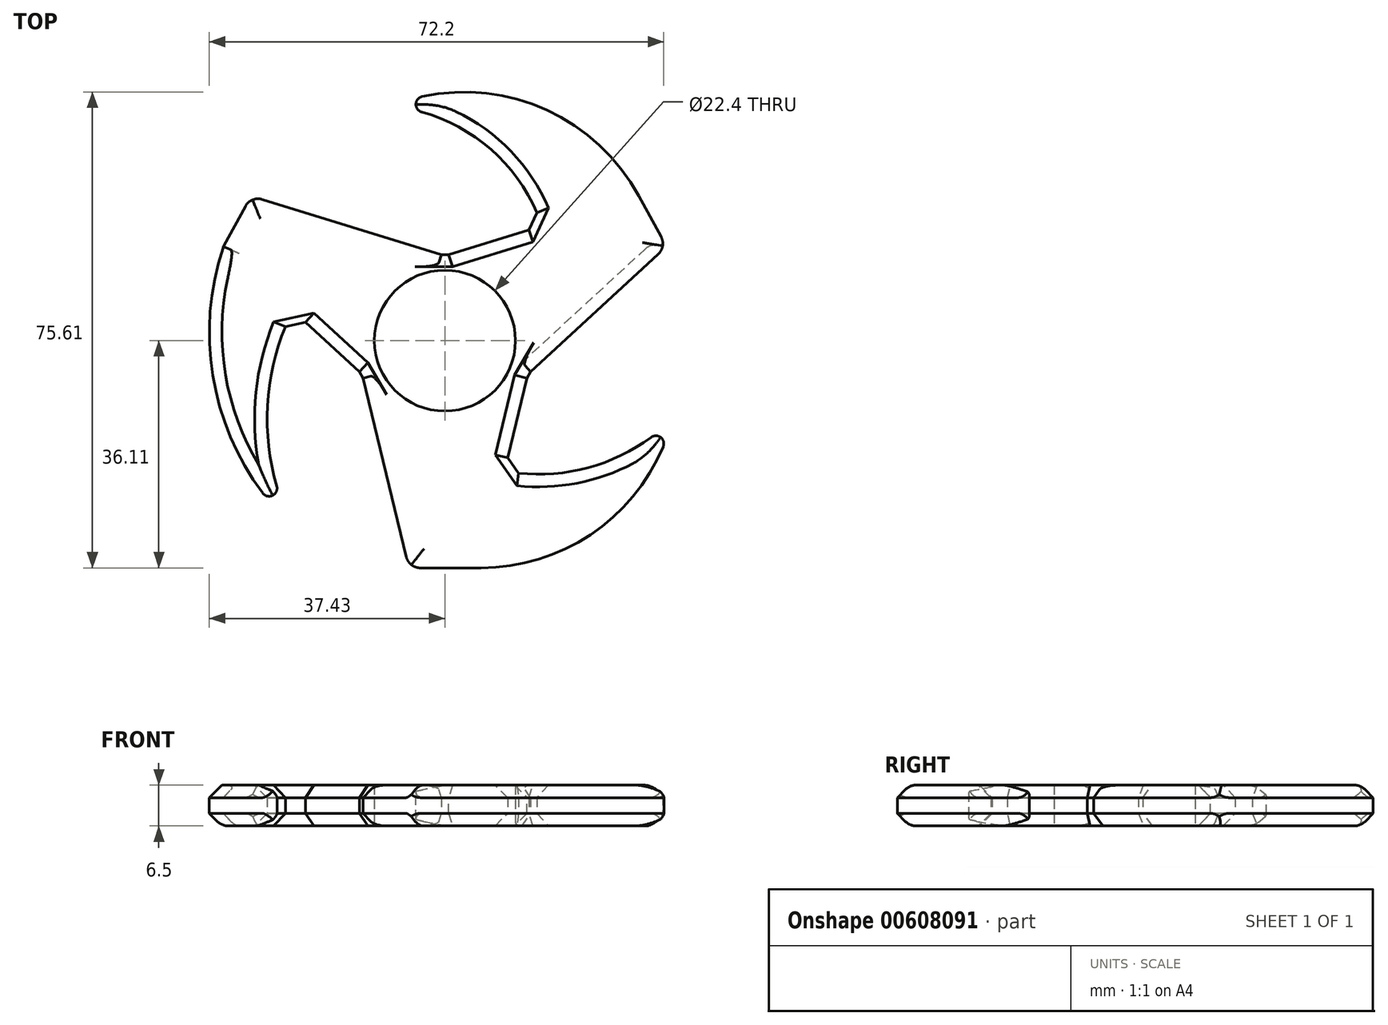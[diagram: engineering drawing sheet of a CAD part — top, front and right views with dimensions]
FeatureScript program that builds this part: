
annotation { "Feature Type Name" : "Feature", "Feature Type Description" : "" }
export const myFeature = defineFeature(function(context is Context, id is Id, definition is map)
    precondition{}
    {
        {
            var Q0;
            Q0=qCreatedBy(makeId("Top.planeOp"),FACE);
            var sketch = newSketch(context, id + "F0", { "sketchPlane" : qUnion([Q0])});
            skCircle(sketch, "E0", {"center": v(0, 0) * mm, "radius": 47.37 * mm});
            skPoint(sketch, "E1.0.midPoint", {"position": v(0, 23) * mm});
            skLineSegment(sketch, "E2", {"start": v(-5.71, -36.1) * mm, "end": v(0, -36.1) * mm});
            skLineSegment(sketch, "E3", {"start": v(-30.81, 23) * mm, "end": v(-35.2, 14.95) * mm});
            skLineSegment(sketch, "E4.MirrorCS", {"start": v(30.81, 23) * mm, "end": v(35.2, 14.95) * mm});
            skLineSegment(sketch, "E5.MirrorCS", {"start": v(5.71, -36.1) * mm, "end": v(0, -36.1) * mm});
            skLineSegment(sketch, "E6", {"start": v(0, -46) * mm, "end": v(0, 0) * mm});
            skLineSegment(sketch, "E7", {"start": v(-13.16, -5.35) * mm, "end": v(-5.71, -36.1) * mm});
            skLineSegment(sketch, "E8", {"start": v(-30.81, 23) * mm, "end": v(0, 13.45) * mm});
            skLineSegment(sketch, "E9", {"start": v(0, 59.17) * mm, "end": v(0, -57.43) * mm, "construction": true});
            skLineSegment(sketch, "E10.MirrorCS", {"start": v(35.2, 14.95) * mm, "end": v(13.16, -5.35) * mm});
            skCircle(sketch, "E11", {"center": v(0, 0) * mm, "radius": 11.2 * mm});
            skArc(sketch, "E12", {"start": v(-24.18, 4.8) * mm, "mid": v(-28.24, -12.41) * mm, "end": v(-24.18, -29.62) * mm});
            skArc(sketch, "E13", {"start": v(-35.2, 14.95) * mm, "mid": v(-36.18, -8.94) * mm, "end": v(-24.18, -29.62) * mm});
            skLineSegment(sketch, "E14", {"start": v(-24.18, 4.8) * mm, "end": v(-13.16, -5.35) * mm});
            skArc(sketch, "E15", {"start": v(9.44, -20.73) * mm, "mid": v(23.83, -19.87) * mm, "end": v(36.17, -12.41) * mm});
            skArc(sketch, "E16", {"start": v(5.71, -36.1) * mm, "mid": v(25, -29.49) * mm, "end": v(36.17, -12.41) * mm});
            skLineSegment(sketch, "E17", {"start": v(9.44, -20.73) * mm, "end": v(13.16, -5.35) * mm});
            skArc(sketch, "E18", {"start": v(15.4, 18.23) * mm, "mid": v(6.18, 31.3) * mm, "end": v(-8.69, 37.24) * mm});
            skArc(sketch, "E19", {"start": v(30.81, 23) * mm, "mid": v(13.77, 37.63) * mm, "end": v(-8.69, 37.24) * mm});
            skLineSegment(sketch, "E20", {"start": v(15.4, 18.23) * mm, "end": v(0, 13.45) * mm});
            skSolve(sketch);
        }
        {
            var Q0;
            Q0=makeQuery(id+"F0.imprint","IMPRINT",FACE,{"disambiguationData":[TD([[makeQuery(id+"F0.imprint","IMPRINT",EDGE,{"derivedFrom":sQuery(id+"F0.wireOp",EDGE,"E2")}),1.0]])]});
            extrude(context, id + "F1", {"entities" : qUnion([Q0]), "depth" : 6.5 * mm, "offsetDistance" : 25.4 * mm});
        }
        {
            var Q0;
            Q0=makeQuery(id+"F1.opExtrude","CAP_EDGE",EDGE,{"disambiguationData":[OSD([sQuery(id+"F0.wireOp",EDGE,"E3")])],"isStart":false});
            var Q1;
            Q1=makeQuery(id+"F1.opExtrude","CAP_EDGE",EDGE,{"disambiguationData":[OSD([sQuery(id+"F0.wireOp",EDGE,"E3")])],"isStart":true});
            var Q2;
            Q2=makeQuery(id+"F1.opExtrude","CAP_EDGE",EDGE,{"disambiguationData":[OSD([sQuery(id+"F0.wireOp",EDGE,"E8")])],"isStart":false});
            var Q3;
            Q3=makeQuery(id+"F1.opExtrude","CAP_EDGE",EDGE,{"disambiguationData":[OSD([sQuery(id+"F0.wireOp",EDGE,"E8")])],"isStart":true});
            var Q4;
            Q4=makeQuery(id+"F1.opExtrude","CAP_EDGE",EDGE,{"disambiguationData":[OSD([sQuery(id+"F0.wireOp",EDGE,"abd28260-5241-46c7-9a49-41b6c746b0a20.MirrorCS")])],"isStart":true});
            var Q5;
            Q5=makeQuery(id+"F1.opExtrude","CAP_EDGE",EDGE,{"disambiguationData":[OSD([sQuery(id+"F0.wireOp",EDGE,"abd28260-5241-46c7-9a49-41b6c746b0a20.MirrorCS")])],"isStart":false});
            var Q6;
            Q6=makeQuery(id+"F1.opExtrude","CAP_EDGE",EDGE,{"disambiguationData":[OSD([sQuery(id+"F0.wireOp",EDGE,"E4.MirrorCS")])],"isStart":false});
            var Q7;
            Q7=makeQuery(id+"F1.opExtrude","CAP_EDGE",EDGE,{"disambiguationData":[OSD([sQuery(id+"F0.wireOp",EDGE,"QS45Ad1f-zS77-PmQo-UpQF-622HsvFARksc")])],"isStart":false});
            var Q8;
            Q8=makeQuery(id+"F1.opExtrude","CAP_EDGE",EDGE,{"disambiguationData":[OSD([sQuery(id+"F0.wireOp",EDGE,"E7")])],"isStart":false});
            var Q9;
            Q9=makeQuery(id+"F1.opExtrude","CAP_EDGE",EDGE,{"disambiguationData":[OSD([sQuery(id+"F0.wireOp",EDGE,"E7")])],"isStart":true});
            var Q10;
            Q10=makeQuery(id+"F1.opExtrude","CAP_EDGE",EDGE,{"disambiguationData":[OSD([sQuery(id+"F0.wireOp",EDGE,"E2"),sQuery(id+"F0.wireOp",EDGE,"E5.MirrorCS")])],"isStart":false});
            var Q11;
            Q11=makeQuery(id+"F1.opExtrude","CAP_EDGE",EDGE,{"disambiguationData":[OSD([sQuery(id+"F0.wireOp",EDGE,"273b9097-7943-4664-901e-a9dfdd62f2f80.MirrorCS")])],"isStart":false});
            var Q12;
            Q12=makeQuery(id+"F1.opExtrude","CAP_EDGE",EDGE,{"disambiguationData":[OSD([sQuery(id+"F0.wireOp",EDGE,"E10.MirrorCS")])],"isStart":false});
            var Q13;
            Q13=makeQuery(id+"F1.opExtrude","CAP_EDGE",EDGE,{"disambiguationData":[OSD([sQuery(id+"F0.wireOp",EDGE,"QS45Ad1f-zS77-PmQo-UpQF-622HsvFARksc")])],"isStart":true});
            var Q14;
            Q14=makeQuery(id+"F1.opExtrude","CAP_EDGE",EDGE,{"disambiguationData":[OSD([sQuery(id+"F0.wireOp",EDGE,"E2"),sQuery(id+"F0.wireOp",EDGE,"E5.MirrorCS")])],"isStart":true});
            var Q15;
            Q15=makeQuery(id+"F1.opExtrude","CAP_EDGE",EDGE,{"disambiguationData":[OSD([sQuery(id+"F0.wireOp",EDGE,"273b9097-7943-4664-901e-a9dfdd62f2f80.MirrorCS")])],"isStart":true});
            var Q16;
            Q16=makeQuery(id+"F1.opExtrude","CAP_EDGE",EDGE,{"disambiguationData":[OSD([sQuery(id+"F0.wireOp",EDGE,"E10.MirrorCS")])],"isStart":true});
            var Q17;
            Q17=makeQuery(id+"F1.opExtrude","CAP_EDGE",EDGE,{"disambiguationData":[OSD([sQuery(id+"F0.wireOp",EDGE,"E4.MirrorCS")])],"isStart":true});
            var Q18;
            Q18=makeQuery(id+"F1.opExtrude","CAP_EDGE",EDGE,{"disambiguationData":[OSD([sQuery(id+"F0.wireOp",EDGE,"E12")])],"isStart":false});
            var Q19;
            Q19=makeQuery(id+"F1.opExtrude","CAP_EDGE",EDGE,{"disambiguationData":[OSD([sQuery(id+"F0.wireOp",EDGE,"E12")])],"isStart":true});
            var Q20;
            Q20=makeQuery(id+"F1.opExtrude","CAP_EDGE",EDGE,{"disambiguationData":[OSD([sQuery(id+"F0.wireOp",EDGE,"E18")])],"isStart":false});
            var Q21;
            Q21=makeQuery(id+"F1.opExtrude","CAP_EDGE",EDGE,{"disambiguationData":[OSD([sQuery(id+"F0.wireOp",EDGE,"E18")])],"isStart":true});
            var Q22;
            Q22=makeQuery(id+"F1.opExtrude","CAP_EDGE",EDGE,{"disambiguationData":[OSD([sQuery(id+"F0.wireOp",EDGE,"E15")])],"isStart":false});
            var Q23;
            Q23=makeQuery(id+"F1.opExtrude","CAP_EDGE",EDGE,{"disambiguationData":[OSD([sQuery(id+"F0.wireOp",EDGE,"E15")])],"isStart":true});
            var Q24;
            Q24=makeQuery(id+"F1.opExtrude","CAP_EDGE",EDGE,{"disambiguationData":[OSD([sQuery(id+"F0.wireOp",EDGE,"E13")])],"isStart":true});
            var Q25;
            Q25=makeQuery(id+"F1.opExtrude","CAP_EDGE",EDGE,{"disambiguationData":[OSD([sQuery(id+"F0.wireOp",EDGE,"E13")])],"isStart":false});
            var Q26;
            Q26=makeQuery(id+"F1.opExtrude","SWEPT_FACE",FACE,{"disambiguationData":[OSD([sQuery(id+"F0.wireOp",EDGE,"E14")])]});
            var Q27;
            Q27=makeQuery(id+"F1.opExtrude","SWEPT_FACE",FACE,{"disambiguationData":[OSD([sQuery(id+"F0.wireOp",EDGE,"E17")])]});
            var Q28;
            Q28=makeQuery(id+"F1.opExtrude","SWEPT_FACE",FACE,{"disambiguationData":[OSD([sQuery(id+"F0.wireOp",EDGE,"E20")])]});
            chamfer(context, id + "F2", {"entities" : qUnion([Q0, Q1, Q2, Q3, Q4, Q5, Q6, Q7, Q8, Q9, Q10, Q11, Q12, Q13, Q14, Q15, Q16, Q17, Q18, Q19, Q20, Q21, Q22, Q23, Q24, Q25, Q26, Q27, Q28]), "width" : 2 * mm, "tangentPropagation" : true});
        }
        {
            var Q0;
            {var subQ0=sQuery(id+"F0.wireOp",EDGE,"E3");Q0=makeQuery(id+"F2.opChamfer","BLEND_EDGE",EDGE,{"blendedFrom":[makeQuery(id+"F1.opExtrude","CAP_EDGE",EDGE,{"disambiguationData":[OSD([subQ0])],"isStart":false}),makeQuery(id+"F1.opExtrude","CAP_FACE",FACE,{"disambiguationData":[OSD([sQuery(id+"F0.wireOp",EDGE,"E2"),subQ0,sQuery(id+"F0.wireOp",EDGE,"E4.MirrorCS"),sQuery(id+"F0.wireOp",EDGE,"E5.MirrorCS"),sQuery(id+"F0.wireOp",EDGE,"QS45Ad1f-zS77-PmQo-UpQF-622HsvFARksc"),sQuery(id+"F0.wireOp",EDGE,"E7"),sQuery(id+"F0.wireOp",EDGE,"E8"),sQuery(id+"F0.wireOp",EDGE,"abd28260-5241-46c7-9a49-41b6c746b0a20.MirrorCS"),sQuery(id+"F0.wireOp",EDGE,"E10.MirrorCS"),sQuery(id+"F0.wireOp",EDGE,"273b9097-7943-4664-901e-a9dfdd62f2f80.MirrorCS"),sQuery(id+"F0.wireOp",EDGE,"E11")])],"isStart":false})],"blendedInto":[makeQuery(id+"F1.opExtrude","CAP_FACE",FACE,{"disambiguationData":[OSD([sQuery(id+"F0.wireOp",EDGE,"E2"),subQ0,sQuery(id+"F0.wireOp",EDGE,"E4.MirrorCS"),sQuery(id+"F0.wireOp",EDGE,"E5.MirrorCS"),sQuery(id+"F0.wireOp",EDGE,"QS45Ad1f-zS77-PmQo-UpQF-622HsvFARksc"),sQuery(id+"F0.wireOp",EDGE,"E7"),sQuery(id+"F0.wireOp",EDGE,"E8"),sQuery(id+"F0.wireOp",EDGE,"abd28260-5241-46c7-9a49-41b6c746b0a20.MirrorCS"),sQuery(id+"F0.wireOp",EDGE,"E10.MirrorCS"),sQuery(id+"F0.wireOp",EDGE,"273b9097-7943-4664-901e-a9dfdd62f2f80.MirrorCS"),sQuery(id+"F0.wireOp",EDGE,"E11")])],"isStart":false})]});}
            var Q1;
            {var subQ0=sQuery(id+"F0.wireOp",EDGE,"abd28260-5241-46c7-9a49-41b6c746b0a20.MirrorCS");Q1=makeQuery(id+"F2.opChamfer","BLEND_EDGE",EDGE,{"blendedFrom":[makeQuery(id+"F1.opExtrude","CAP_EDGE",EDGE,{"disambiguationData":[OSD([subQ0])],"isStart":false}),makeQuery(id+"F1.opExtrude","CAP_FACE",FACE,{"disambiguationData":[OSD([sQuery(id+"F0.wireOp",EDGE,"E2"),sQuery(id+"F0.wireOp",EDGE,"E3"),sQuery(id+"F0.wireOp",EDGE,"E4.MirrorCS"),sQuery(id+"F0.wireOp",EDGE,"E5.MirrorCS"),sQuery(id+"F0.wireOp",EDGE,"QS45Ad1f-zS77-PmQo-UpQF-622HsvFARksc"),sQuery(id+"F0.wireOp",EDGE,"E7"),sQuery(id+"F0.wireOp",EDGE,"E8"),subQ0,sQuery(id+"F0.wireOp",EDGE,"E10.MirrorCS"),sQuery(id+"F0.wireOp",EDGE,"273b9097-7943-4664-901e-a9dfdd62f2f80.MirrorCS"),sQuery(id+"F0.wireOp",EDGE,"E11")])],"isStart":false})],"blendedInto":[makeQuery(id+"F1.opExtrude","CAP_FACE",FACE,{"disambiguationData":[OSD([sQuery(id+"F0.wireOp",EDGE,"E2"),sQuery(id+"F0.wireOp",EDGE,"E3"),sQuery(id+"F0.wireOp",EDGE,"E4.MirrorCS"),sQuery(id+"F0.wireOp",EDGE,"E5.MirrorCS"),sQuery(id+"F0.wireOp",EDGE,"QS45Ad1f-zS77-PmQo-UpQF-622HsvFARksc"),sQuery(id+"F0.wireOp",EDGE,"E7"),sQuery(id+"F0.wireOp",EDGE,"E8"),subQ0,sQuery(id+"F0.wireOp",EDGE,"E10.MirrorCS"),sQuery(id+"F0.wireOp",EDGE,"273b9097-7943-4664-901e-a9dfdd62f2f80.MirrorCS"),sQuery(id+"F0.wireOp",EDGE,"E11")])],"isStart":false})]});}
            var Q2;
            {var subQ0=sQuery(id+"F0.wireOp",EDGE,"E8");Q2=makeQuery(id+"F2.opChamfer","BLEND_EDGE",EDGE,{"blendedFrom":[makeQuery(id+"F1.opExtrude","CAP_EDGE",EDGE,{"disambiguationData":[OSD([subQ0])],"isStart":false}),makeQuery(id+"F1.opExtrude","CAP_FACE",FACE,{"disambiguationData":[OSD([sQuery(id+"F0.wireOp",EDGE,"E2"),sQuery(id+"F0.wireOp",EDGE,"E3"),sQuery(id+"F0.wireOp",EDGE,"E4.MirrorCS"),sQuery(id+"F0.wireOp",EDGE,"E5.MirrorCS"),sQuery(id+"F0.wireOp",EDGE,"QS45Ad1f-zS77-PmQo-UpQF-622HsvFARksc"),sQuery(id+"F0.wireOp",EDGE,"E7"),subQ0,sQuery(id+"F0.wireOp",EDGE,"abd28260-5241-46c7-9a49-41b6c746b0a20.MirrorCS"),sQuery(id+"F0.wireOp",EDGE,"E10.MirrorCS"),sQuery(id+"F0.wireOp",EDGE,"273b9097-7943-4664-901e-a9dfdd62f2f80.MirrorCS"),sQuery(id+"F0.wireOp",EDGE,"E11")])],"isStart":false})],"blendedInto":[makeQuery(id+"F1.opExtrude","CAP_FACE",FACE,{"disambiguationData":[OSD([sQuery(id+"F0.wireOp",EDGE,"E2"),sQuery(id+"F0.wireOp",EDGE,"E3"),sQuery(id+"F0.wireOp",EDGE,"E4.MirrorCS"),sQuery(id+"F0.wireOp",EDGE,"E5.MirrorCS"),sQuery(id+"F0.wireOp",EDGE,"QS45Ad1f-zS77-PmQo-UpQF-622HsvFARksc"),sQuery(id+"F0.wireOp",EDGE,"E7"),subQ0,sQuery(id+"F0.wireOp",EDGE,"abd28260-5241-46c7-9a49-41b6c746b0a20.MirrorCS"),sQuery(id+"F0.wireOp",EDGE,"E10.MirrorCS"),sQuery(id+"F0.wireOp",EDGE,"273b9097-7943-4664-901e-a9dfdd62f2f80.MirrorCS"),sQuery(id+"F0.wireOp",EDGE,"E11")])],"isStart":false})]});}
            var Q3;
            {var subQ0=sQuery(id+"F0.wireOp",EDGE,"E10.MirrorCS");Q3=makeQuery(id+"F2.opChamfer","BLEND_EDGE",EDGE,{"blendedFrom":[makeQuery(id+"F1.opExtrude","CAP_EDGE",EDGE,{"disambiguationData":[OSD([subQ0])],"isStart":false}),makeQuery(id+"F1.opExtrude","CAP_FACE",FACE,{"disambiguationData":[OSD([sQuery(id+"F0.wireOp",EDGE,"E2"),sQuery(id+"F0.wireOp",EDGE,"E3"),sQuery(id+"F0.wireOp",EDGE,"E4.MirrorCS"),sQuery(id+"F0.wireOp",EDGE,"E5.MirrorCS"),sQuery(id+"F0.wireOp",EDGE,"QS45Ad1f-zS77-PmQo-UpQF-622HsvFARksc"),sQuery(id+"F0.wireOp",EDGE,"E7"),sQuery(id+"F0.wireOp",EDGE,"E8"),sQuery(id+"F0.wireOp",EDGE,"abd28260-5241-46c7-9a49-41b6c746b0a20.MirrorCS"),subQ0,sQuery(id+"F0.wireOp",EDGE,"273b9097-7943-4664-901e-a9dfdd62f2f80.MirrorCS"),sQuery(id+"F0.wireOp",EDGE,"E11")])],"isStart":false})],"blendedInto":[makeQuery(id+"F1.opExtrude","CAP_FACE",FACE,{"disambiguationData":[OSD([sQuery(id+"F0.wireOp",EDGE,"E2"),sQuery(id+"F0.wireOp",EDGE,"E3"),sQuery(id+"F0.wireOp",EDGE,"E4.MirrorCS"),sQuery(id+"F0.wireOp",EDGE,"E5.MirrorCS"),sQuery(id+"F0.wireOp",EDGE,"QS45Ad1f-zS77-PmQo-UpQF-622HsvFARksc"),sQuery(id+"F0.wireOp",EDGE,"E7"),sQuery(id+"F0.wireOp",EDGE,"E8"),sQuery(id+"F0.wireOp",EDGE,"abd28260-5241-46c7-9a49-41b6c746b0a20.MirrorCS"),subQ0,sQuery(id+"F0.wireOp",EDGE,"273b9097-7943-4664-901e-a9dfdd62f2f80.MirrorCS"),sQuery(id+"F0.wireOp",EDGE,"E11")])],"isStart":false})]});}
            var Q4;
            {var subQ0=sQuery(id+"F0.wireOp",EDGE,"273b9097-7943-4664-901e-a9dfdd62f2f80.MirrorCS");Q4=makeQuery(id+"F2.opChamfer","BLEND_EDGE",EDGE,{"blendedFrom":[makeQuery(id+"F1.opExtrude","CAP_EDGE",EDGE,{"disambiguationData":[OSD([subQ0])],"isStart":false}),makeQuery(id+"F1.opExtrude","CAP_FACE",FACE,{"disambiguationData":[OSD([sQuery(id+"F0.wireOp",EDGE,"E2"),sQuery(id+"F0.wireOp",EDGE,"E3"),sQuery(id+"F0.wireOp",EDGE,"E4.MirrorCS"),sQuery(id+"F0.wireOp",EDGE,"E5.MirrorCS"),sQuery(id+"F0.wireOp",EDGE,"QS45Ad1f-zS77-PmQo-UpQF-622HsvFARksc"),sQuery(id+"F0.wireOp",EDGE,"E7"),sQuery(id+"F0.wireOp",EDGE,"E8"),sQuery(id+"F0.wireOp",EDGE,"abd28260-5241-46c7-9a49-41b6c746b0a20.MirrorCS"),sQuery(id+"F0.wireOp",EDGE,"E10.MirrorCS"),subQ0,sQuery(id+"F0.wireOp",EDGE,"E11")])],"isStart":false})],"blendedInto":[makeQuery(id+"F1.opExtrude","CAP_FACE",FACE,{"disambiguationData":[OSD([sQuery(id+"F0.wireOp",EDGE,"E2"),sQuery(id+"F0.wireOp",EDGE,"E3"),sQuery(id+"F0.wireOp",EDGE,"E4.MirrorCS"),sQuery(id+"F0.wireOp",EDGE,"E5.MirrorCS"),sQuery(id+"F0.wireOp",EDGE,"QS45Ad1f-zS77-PmQo-UpQF-622HsvFARksc"),sQuery(id+"F0.wireOp",EDGE,"E7"),sQuery(id+"F0.wireOp",EDGE,"E8"),sQuery(id+"F0.wireOp",EDGE,"abd28260-5241-46c7-9a49-41b6c746b0a20.MirrorCS"),sQuery(id+"F0.wireOp",EDGE,"E10.MirrorCS"),subQ0,sQuery(id+"F0.wireOp",EDGE,"E11")])],"isStart":false})]});}
            var Q5;
            {var subQ0=sQuery(id+"F0.wireOp",EDGE,"E7");Q5=makeQuery(id+"F2.opChamfer","BLEND_EDGE",EDGE,{"blendedFrom":[makeQuery(id+"F1.opExtrude","CAP_EDGE",EDGE,{"disambiguationData":[OSD([subQ0])],"isStart":false}),makeQuery(id+"F1.opExtrude","CAP_FACE",FACE,{"disambiguationData":[OSD([sQuery(id+"F0.wireOp",EDGE,"E2"),sQuery(id+"F0.wireOp",EDGE,"E3"),sQuery(id+"F0.wireOp",EDGE,"E4.MirrorCS"),sQuery(id+"F0.wireOp",EDGE,"E5.MirrorCS"),sQuery(id+"F0.wireOp",EDGE,"QS45Ad1f-zS77-PmQo-UpQF-622HsvFARksc"),subQ0,sQuery(id+"F0.wireOp",EDGE,"E8"),sQuery(id+"F0.wireOp",EDGE,"abd28260-5241-46c7-9a49-41b6c746b0a20.MirrorCS"),sQuery(id+"F0.wireOp",EDGE,"E10.MirrorCS"),sQuery(id+"F0.wireOp",EDGE,"273b9097-7943-4664-901e-a9dfdd62f2f80.MirrorCS"),sQuery(id+"F0.wireOp",EDGE,"E11")])],"isStart":false})],"blendedInto":[makeQuery(id+"F1.opExtrude","CAP_FACE",FACE,{"disambiguationData":[OSD([sQuery(id+"F0.wireOp",EDGE,"E2"),sQuery(id+"F0.wireOp",EDGE,"E3"),sQuery(id+"F0.wireOp",EDGE,"E4.MirrorCS"),sQuery(id+"F0.wireOp",EDGE,"E5.MirrorCS"),sQuery(id+"F0.wireOp",EDGE,"QS45Ad1f-zS77-PmQo-UpQF-622HsvFARksc"),subQ0,sQuery(id+"F0.wireOp",EDGE,"E8"),sQuery(id+"F0.wireOp",EDGE,"abd28260-5241-46c7-9a49-41b6c746b0a20.MirrorCS"),sQuery(id+"F0.wireOp",EDGE,"E10.MirrorCS"),sQuery(id+"F0.wireOp",EDGE,"273b9097-7943-4664-901e-a9dfdd62f2f80.MirrorCS"),sQuery(id+"F0.wireOp",EDGE,"E11")])],"isStart":false})]});}
            var Q6;
            {var subQ0=sQuery(id+"F0.wireOp",EDGE,"QS45Ad1f-zS77-PmQo-UpQF-622HsvFARksc");Q6=makeQuery(id+"F2.opChamfer","BLEND_EDGE",EDGE,{"blendedFrom":[makeQuery(id+"F1.opExtrude","CAP_EDGE",EDGE,{"disambiguationData":[OSD([subQ0])],"isStart":false}),makeQuery(id+"F1.opExtrude","CAP_FACE",FACE,{"disambiguationData":[OSD([sQuery(id+"F0.wireOp",EDGE,"E2"),sQuery(id+"F0.wireOp",EDGE,"E3"),sQuery(id+"F0.wireOp",EDGE,"E4.MirrorCS"),sQuery(id+"F0.wireOp",EDGE,"E5.MirrorCS"),subQ0,sQuery(id+"F0.wireOp",EDGE,"E7"),sQuery(id+"F0.wireOp",EDGE,"E8"),sQuery(id+"F0.wireOp",EDGE,"abd28260-5241-46c7-9a49-41b6c746b0a20.MirrorCS"),sQuery(id+"F0.wireOp",EDGE,"E10.MirrorCS"),sQuery(id+"F0.wireOp",EDGE,"273b9097-7943-4664-901e-a9dfdd62f2f80.MirrorCS"),sQuery(id+"F0.wireOp",EDGE,"E11")])],"isStart":false})],"blendedInto":[makeQuery(id+"F1.opExtrude","CAP_FACE",FACE,{"disambiguationData":[OSD([sQuery(id+"F0.wireOp",EDGE,"E2"),sQuery(id+"F0.wireOp",EDGE,"E3"),sQuery(id+"F0.wireOp",EDGE,"E4.MirrorCS"),sQuery(id+"F0.wireOp",EDGE,"E5.MirrorCS"),subQ0,sQuery(id+"F0.wireOp",EDGE,"E7"),sQuery(id+"F0.wireOp",EDGE,"E8"),sQuery(id+"F0.wireOp",EDGE,"abd28260-5241-46c7-9a49-41b6c746b0a20.MirrorCS"),sQuery(id+"F0.wireOp",EDGE,"E10.MirrorCS"),sQuery(id+"F0.wireOp",EDGE,"273b9097-7943-4664-901e-a9dfdd62f2f80.MirrorCS"),sQuery(id+"F0.wireOp",EDGE,"E11")])],"isStart":false})]});}
            var Q7;
            {var subQ0=sQuery(id+"F0.wireOp",EDGE,"E4.MirrorCS");Q7=makeQuery(id+"F2.opChamfer","BLEND_EDGE",EDGE,{"blendedFrom":[makeQuery(id+"F1.opExtrude","CAP_EDGE",EDGE,{"disambiguationData":[OSD([subQ0])],"isStart":false}),makeQuery(id+"F1.opExtrude","CAP_FACE",FACE,{"disambiguationData":[OSD([sQuery(id+"F0.wireOp",EDGE,"E2"),sQuery(id+"F0.wireOp",EDGE,"E3"),subQ0,sQuery(id+"F0.wireOp",EDGE,"E5.MirrorCS"),sQuery(id+"F0.wireOp",EDGE,"QS45Ad1f-zS77-PmQo-UpQF-622HsvFARksc"),sQuery(id+"F0.wireOp",EDGE,"E7"),sQuery(id+"F0.wireOp",EDGE,"E8"),sQuery(id+"F0.wireOp",EDGE,"abd28260-5241-46c7-9a49-41b6c746b0a20.MirrorCS"),sQuery(id+"F0.wireOp",EDGE,"E10.MirrorCS"),sQuery(id+"F0.wireOp",EDGE,"273b9097-7943-4664-901e-a9dfdd62f2f80.MirrorCS"),sQuery(id+"F0.wireOp",EDGE,"E11")])],"isStart":false})],"blendedInto":[makeQuery(id+"F1.opExtrude","CAP_FACE",FACE,{"disambiguationData":[OSD([sQuery(id+"F0.wireOp",EDGE,"E2"),sQuery(id+"F0.wireOp",EDGE,"E3"),subQ0,sQuery(id+"F0.wireOp",EDGE,"E5.MirrorCS"),sQuery(id+"F0.wireOp",EDGE,"QS45Ad1f-zS77-PmQo-UpQF-622HsvFARksc"),sQuery(id+"F0.wireOp",EDGE,"E7"),sQuery(id+"F0.wireOp",EDGE,"E8"),sQuery(id+"F0.wireOp",EDGE,"abd28260-5241-46c7-9a49-41b6c746b0a20.MirrorCS"),sQuery(id+"F0.wireOp",EDGE,"E10.MirrorCS"),sQuery(id+"F0.wireOp",EDGE,"273b9097-7943-4664-901e-a9dfdd62f2f80.MirrorCS"),sQuery(id+"F0.wireOp",EDGE,"E11")])],"isStart":false})]});}
            var Q8;
            {var subQ0=sQuery(id+"F0.wireOp",EDGE,"E5.MirrorCS");var subQ1=sQuery(id+"F0.wireOp",EDGE,"E2");Q8=makeQuery(id+"F2.opChamfer","BLEND_EDGE",EDGE,{"blendedFrom":[makeQuery(id+"F1.opExtrude","CAP_EDGE",EDGE,{"disambiguationData":[OSD([subQ1,subQ0])],"isStart":false}),makeQuery(id+"F1.opExtrude","CAP_FACE",FACE,{"disambiguationData":[OSD([subQ1,sQuery(id+"F0.wireOp",EDGE,"E3"),sQuery(id+"F0.wireOp",EDGE,"E4.MirrorCS"),subQ0,sQuery(id+"F0.wireOp",EDGE,"QS45Ad1f-zS77-PmQo-UpQF-622HsvFARksc"),sQuery(id+"F0.wireOp",EDGE,"E7"),sQuery(id+"F0.wireOp",EDGE,"E8"),sQuery(id+"F0.wireOp",EDGE,"abd28260-5241-46c7-9a49-41b6c746b0a20.MirrorCS"),sQuery(id+"F0.wireOp",EDGE,"E10.MirrorCS"),sQuery(id+"F0.wireOp",EDGE,"273b9097-7943-4664-901e-a9dfdd62f2f80.MirrorCS"),sQuery(id+"F0.wireOp",EDGE,"E11")])],"isStart":false})],"blendedInto":[makeQuery(id+"F1.opExtrude","CAP_FACE",FACE,{"disambiguationData":[OSD([subQ1,sQuery(id+"F0.wireOp",EDGE,"E3"),sQuery(id+"F0.wireOp",EDGE,"E4.MirrorCS"),subQ0,sQuery(id+"F0.wireOp",EDGE,"QS45Ad1f-zS77-PmQo-UpQF-622HsvFARksc"),sQuery(id+"F0.wireOp",EDGE,"E7"),sQuery(id+"F0.wireOp",EDGE,"E8"),sQuery(id+"F0.wireOp",EDGE,"abd28260-5241-46c7-9a49-41b6c746b0a20.MirrorCS"),sQuery(id+"F0.wireOp",EDGE,"E10.MirrorCS"),sQuery(id+"F0.wireOp",EDGE,"273b9097-7943-4664-901e-a9dfdd62f2f80.MirrorCS"),sQuery(id+"F0.wireOp",EDGE,"E11")])],"isStart":false})]});}
            var Q9;
            {var subQ0=sQuery(id+"F0.wireOp",EDGE,"E4.MirrorCS");Q9=makeQuery(id+"F2.opChamfer","BLEND_EDGE",EDGE,{"blendedFrom":[makeQuery(id+"F1.opExtrude","CAP_EDGE",EDGE,{"disambiguationData":[OSD([subQ0])],"isStart":true}),makeQuery(id+"F1.opExtrude","CAP_FACE",FACE,{"disambiguationData":[OSD([sQuery(id+"F0.wireOp",EDGE,"E2"),sQuery(id+"F0.wireOp",EDGE,"E3"),subQ0,sQuery(id+"F0.wireOp",EDGE,"E5.MirrorCS"),sQuery(id+"F0.wireOp",EDGE,"QS45Ad1f-zS77-PmQo-UpQF-622HsvFARksc"),sQuery(id+"F0.wireOp",EDGE,"E7"),sQuery(id+"F0.wireOp",EDGE,"E8"),sQuery(id+"F0.wireOp",EDGE,"abd28260-5241-46c7-9a49-41b6c746b0a20.MirrorCS"),sQuery(id+"F0.wireOp",EDGE,"E10.MirrorCS"),sQuery(id+"F0.wireOp",EDGE,"273b9097-7943-4664-901e-a9dfdd62f2f80.MirrorCS"),sQuery(id+"F0.wireOp",EDGE,"E11")])],"isStart":true})],"blendedInto":[makeQuery(id+"F1.opExtrude","CAP_FACE",FACE,{"disambiguationData":[OSD([sQuery(id+"F0.wireOp",EDGE,"E2"),sQuery(id+"F0.wireOp",EDGE,"E3"),subQ0,sQuery(id+"F0.wireOp",EDGE,"E5.MirrorCS"),sQuery(id+"F0.wireOp",EDGE,"QS45Ad1f-zS77-PmQo-UpQF-622HsvFARksc"),sQuery(id+"F0.wireOp",EDGE,"E7"),sQuery(id+"F0.wireOp",EDGE,"E8"),sQuery(id+"F0.wireOp",EDGE,"abd28260-5241-46c7-9a49-41b6c746b0a20.MirrorCS"),sQuery(id+"F0.wireOp",EDGE,"E10.MirrorCS"),sQuery(id+"F0.wireOp",EDGE,"273b9097-7943-4664-901e-a9dfdd62f2f80.MirrorCS"),sQuery(id+"F0.wireOp",EDGE,"E11")])],"isStart":true})]});}
            var Q10;
            {var subQ0=sQuery(id+"F0.wireOp",EDGE,"abd28260-5241-46c7-9a49-41b6c746b0a20.MirrorCS");Q10=makeQuery(id+"F2.opChamfer","BLEND_EDGE",EDGE,{"blendedFrom":[makeQuery(id+"F1.opExtrude","CAP_EDGE",EDGE,{"disambiguationData":[OSD([subQ0])],"isStart":true}),makeQuery(id+"F1.opExtrude","CAP_FACE",FACE,{"disambiguationData":[OSD([sQuery(id+"F0.wireOp",EDGE,"E2"),sQuery(id+"F0.wireOp",EDGE,"E3"),sQuery(id+"F0.wireOp",EDGE,"E4.MirrorCS"),sQuery(id+"F0.wireOp",EDGE,"E5.MirrorCS"),sQuery(id+"F0.wireOp",EDGE,"QS45Ad1f-zS77-PmQo-UpQF-622HsvFARksc"),sQuery(id+"F0.wireOp",EDGE,"E7"),sQuery(id+"F0.wireOp",EDGE,"E8"),subQ0,sQuery(id+"F0.wireOp",EDGE,"E10.MirrorCS"),sQuery(id+"F0.wireOp",EDGE,"273b9097-7943-4664-901e-a9dfdd62f2f80.MirrorCS"),sQuery(id+"F0.wireOp",EDGE,"E11")])],"isStart":true})],"blendedInto":[makeQuery(id+"F1.opExtrude","CAP_FACE",FACE,{"disambiguationData":[OSD([sQuery(id+"F0.wireOp",EDGE,"E2"),sQuery(id+"F0.wireOp",EDGE,"E3"),sQuery(id+"F0.wireOp",EDGE,"E4.MirrorCS"),sQuery(id+"F0.wireOp",EDGE,"E5.MirrorCS"),sQuery(id+"F0.wireOp",EDGE,"QS45Ad1f-zS77-PmQo-UpQF-622HsvFARksc"),sQuery(id+"F0.wireOp",EDGE,"E7"),sQuery(id+"F0.wireOp",EDGE,"E8"),subQ0,sQuery(id+"F0.wireOp",EDGE,"E10.MirrorCS"),sQuery(id+"F0.wireOp",EDGE,"273b9097-7943-4664-901e-a9dfdd62f2f80.MirrorCS"),sQuery(id+"F0.wireOp",EDGE,"E11")])],"isStart":true})]});}
            var Q11;
            {var subQ0=sQuery(id+"F0.wireOp",EDGE,"E8");Q11=makeQuery(id+"F2.opChamfer","BLEND_EDGE",EDGE,{"blendedFrom":[makeQuery(id+"F1.opExtrude","CAP_EDGE",EDGE,{"disambiguationData":[OSD([subQ0])],"isStart":true}),makeQuery(id+"F1.opExtrude","CAP_FACE",FACE,{"disambiguationData":[OSD([sQuery(id+"F0.wireOp",EDGE,"E2"),sQuery(id+"F0.wireOp",EDGE,"E3"),sQuery(id+"F0.wireOp",EDGE,"E4.MirrorCS"),sQuery(id+"F0.wireOp",EDGE,"E5.MirrorCS"),sQuery(id+"F0.wireOp",EDGE,"QS45Ad1f-zS77-PmQo-UpQF-622HsvFARksc"),sQuery(id+"F0.wireOp",EDGE,"E7"),subQ0,sQuery(id+"F0.wireOp",EDGE,"abd28260-5241-46c7-9a49-41b6c746b0a20.MirrorCS"),sQuery(id+"F0.wireOp",EDGE,"E10.MirrorCS"),sQuery(id+"F0.wireOp",EDGE,"273b9097-7943-4664-901e-a9dfdd62f2f80.MirrorCS"),sQuery(id+"F0.wireOp",EDGE,"E11")])],"isStart":true})],"blendedInto":[makeQuery(id+"F1.opExtrude","CAP_FACE",FACE,{"disambiguationData":[OSD([sQuery(id+"F0.wireOp",EDGE,"E2"),sQuery(id+"F0.wireOp",EDGE,"E3"),sQuery(id+"F0.wireOp",EDGE,"E4.MirrorCS"),sQuery(id+"F0.wireOp",EDGE,"E5.MirrorCS"),sQuery(id+"F0.wireOp",EDGE,"QS45Ad1f-zS77-PmQo-UpQF-622HsvFARksc"),sQuery(id+"F0.wireOp",EDGE,"E7"),subQ0,sQuery(id+"F0.wireOp",EDGE,"abd28260-5241-46c7-9a49-41b6c746b0a20.MirrorCS"),sQuery(id+"F0.wireOp",EDGE,"E10.MirrorCS"),sQuery(id+"F0.wireOp",EDGE,"273b9097-7943-4664-901e-a9dfdd62f2f80.MirrorCS"),sQuery(id+"F0.wireOp",EDGE,"E11")])],"isStart":true})]});}
            var Q12;
            {var subQ0=sQuery(id+"F0.wireOp",EDGE,"QS45Ad1f-zS77-PmQo-UpQF-622HsvFARksc");Q12=makeQuery(id+"F2.opChamfer","BLEND_EDGE",EDGE,{"blendedFrom":[makeQuery(id+"F1.opExtrude","CAP_EDGE",EDGE,{"disambiguationData":[OSD([subQ0])],"isStart":true}),makeQuery(id+"F1.opExtrude","CAP_FACE",FACE,{"disambiguationData":[OSD([sQuery(id+"F0.wireOp",EDGE,"E2"),sQuery(id+"F0.wireOp",EDGE,"E3"),sQuery(id+"F0.wireOp",EDGE,"E4.MirrorCS"),sQuery(id+"F0.wireOp",EDGE,"E5.MirrorCS"),subQ0,sQuery(id+"F0.wireOp",EDGE,"E7"),sQuery(id+"F0.wireOp",EDGE,"E8"),sQuery(id+"F0.wireOp",EDGE,"abd28260-5241-46c7-9a49-41b6c746b0a20.MirrorCS"),sQuery(id+"F0.wireOp",EDGE,"E10.MirrorCS"),sQuery(id+"F0.wireOp",EDGE,"273b9097-7943-4664-901e-a9dfdd62f2f80.MirrorCS"),sQuery(id+"F0.wireOp",EDGE,"E11")])],"isStart":true})],"blendedInto":[makeQuery(id+"F1.opExtrude","CAP_FACE",FACE,{"disambiguationData":[OSD([sQuery(id+"F0.wireOp",EDGE,"E2"),sQuery(id+"F0.wireOp",EDGE,"E3"),sQuery(id+"F0.wireOp",EDGE,"E4.MirrorCS"),sQuery(id+"F0.wireOp",EDGE,"E5.MirrorCS"),subQ0,sQuery(id+"F0.wireOp",EDGE,"E7"),sQuery(id+"F0.wireOp",EDGE,"E8"),sQuery(id+"F0.wireOp",EDGE,"abd28260-5241-46c7-9a49-41b6c746b0a20.MirrorCS"),sQuery(id+"F0.wireOp",EDGE,"E10.MirrorCS"),sQuery(id+"F0.wireOp",EDGE,"273b9097-7943-4664-901e-a9dfdd62f2f80.MirrorCS"),sQuery(id+"F0.wireOp",EDGE,"E11")])],"isStart":true})]});}
            var Q13;
            {var subQ0=sQuery(id+"F0.wireOp",EDGE,"E3");Q13=makeQuery(id+"F2.opChamfer","BLEND_EDGE",EDGE,{"blendedFrom":[makeQuery(id+"F1.opExtrude","CAP_EDGE",EDGE,{"disambiguationData":[OSD([subQ0])],"isStart":true}),makeQuery(id+"F1.opExtrude","CAP_FACE",FACE,{"disambiguationData":[OSD([sQuery(id+"F0.wireOp",EDGE,"E2"),subQ0,sQuery(id+"F0.wireOp",EDGE,"E4.MirrorCS"),sQuery(id+"F0.wireOp",EDGE,"E5.MirrorCS"),sQuery(id+"F0.wireOp",EDGE,"QS45Ad1f-zS77-PmQo-UpQF-622HsvFARksc"),sQuery(id+"F0.wireOp",EDGE,"E7"),sQuery(id+"F0.wireOp",EDGE,"E8"),sQuery(id+"F0.wireOp",EDGE,"abd28260-5241-46c7-9a49-41b6c746b0a20.MirrorCS"),sQuery(id+"F0.wireOp",EDGE,"E10.MirrorCS"),sQuery(id+"F0.wireOp",EDGE,"273b9097-7943-4664-901e-a9dfdd62f2f80.MirrorCS"),sQuery(id+"F0.wireOp",EDGE,"E11")])],"isStart":true})],"blendedInto":[makeQuery(id+"F1.opExtrude","CAP_FACE",FACE,{"disambiguationData":[OSD([sQuery(id+"F0.wireOp",EDGE,"E2"),subQ0,sQuery(id+"F0.wireOp",EDGE,"E4.MirrorCS"),sQuery(id+"F0.wireOp",EDGE,"E5.MirrorCS"),sQuery(id+"F0.wireOp",EDGE,"QS45Ad1f-zS77-PmQo-UpQF-622HsvFARksc"),sQuery(id+"F0.wireOp",EDGE,"E7"),sQuery(id+"F0.wireOp",EDGE,"E8"),sQuery(id+"F0.wireOp",EDGE,"abd28260-5241-46c7-9a49-41b6c746b0a20.MirrorCS"),sQuery(id+"F0.wireOp",EDGE,"E10.MirrorCS"),sQuery(id+"F0.wireOp",EDGE,"273b9097-7943-4664-901e-a9dfdd62f2f80.MirrorCS"),sQuery(id+"F0.wireOp",EDGE,"E11")])],"isStart":true})]});}
            var Q14;
            {var subQ0=sQuery(id+"F0.wireOp",EDGE,"E7");Q14=makeQuery(id+"F2.opChamfer","BLEND_EDGE",EDGE,{"blendedFrom":[makeQuery(id+"F1.opExtrude","CAP_EDGE",EDGE,{"disambiguationData":[OSD([subQ0])],"isStart":true}),makeQuery(id+"F1.opExtrude","CAP_FACE",FACE,{"disambiguationData":[OSD([sQuery(id+"F0.wireOp",EDGE,"E2"),sQuery(id+"F0.wireOp",EDGE,"E3"),sQuery(id+"F0.wireOp",EDGE,"E4.MirrorCS"),sQuery(id+"F0.wireOp",EDGE,"E5.MirrorCS"),sQuery(id+"F0.wireOp",EDGE,"QS45Ad1f-zS77-PmQo-UpQF-622HsvFARksc"),subQ0,sQuery(id+"F0.wireOp",EDGE,"E8"),sQuery(id+"F0.wireOp",EDGE,"abd28260-5241-46c7-9a49-41b6c746b0a20.MirrorCS"),sQuery(id+"F0.wireOp",EDGE,"E10.MirrorCS"),sQuery(id+"F0.wireOp",EDGE,"273b9097-7943-4664-901e-a9dfdd62f2f80.MirrorCS"),sQuery(id+"F0.wireOp",EDGE,"E11")])],"isStart":true})],"blendedInto":[makeQuery(id+"F1.opExtrude","CAP_FACE",FACE,{"disambiguationData":[OSD([sQuery(id+"F0.wireOp",EDGE,"E2"),sQuery(id+"F0.wireOp",EDGE,"E3"),sQuery(id+"F0.wireOp",EDGE,"E4.MirrorCS"),sQuery(id+"F0.wireOp",EDGE,"E5.MirrorCS"),sQuery(id+"F0.wireOp",EDGE,"QS45Ad1f-zS77-PmQo-UpQF-622HsvFARksc"),subQ0,sQuery(id+"F0.wireOp",EDGE,"E8"),sQuery(id+"F0.wireOp",EDGE,"abd28260-5241-46c7-9a49-41b6c746b0a20.MirrorCS"),sQuery(id+"F0.wireOp",EDGE,"E10.MirrorCS"),sQuery(id+"F0.wireOp",EDGE,"273b9097-7943-4664-901e-a9dfdd62f2f80.MirrorCS"),sQuery(id+"F0.wireOp",EDGE,"E11")])],"isStart":true})]});}
            var Q15;
            {var subQ0=sQuery(id+"F0.wireOp",EDGE,"E5.MirrorCS");var subQ1=sQuery(id+"F0.wireOp",EDGE,"E2");Q15=makeQuery(id+"F2.opChamfer","BLEND_EDGE",EDGE,{"blendedFrom":[makeQuery(id+"F1.opExtrude","CAP_EDGE",EDGE,{"disambiguationData":[OSD([subQ1,subQ0])],"isStart":true}),makeQuery(id+"F1.opExtrude","CAP_FACE",FACE,{"disambiguationData":[OSD([subQ1,sQuery(id+"F0.wireOp",EDGE,"E3"),sQuery(id+"F0.wireOp",EDGE,"E4.MirrorCS"),subQ0,sQuery(id+"F0.wireOp",EDGE,"QS45Ad1f-zS77-PmQo-UpQF-622HsvFARksc"),sQuery(id+"F0.wireOp",EDGE,"E7"),sQuery(id+"F0.wireOp",EDGE,"E8"),sQuery(id+"F0.wireOp",EDGE,"abd28260-5241-46c7-9a49-41b6c746b0a20.MirrorCS"),sQuery(id+"F0.wireOp",EDGE,"E10.MirrorCS"),sQuery(id+"F0.wireOp",EDGE,"273b9097-7943-4664-901e-a9dfdd62f2f80.MirrorCS"),sQuery(id+"F0.wireOp",EDGE,"E11")])],"isStart":true})],"blendedInto":[makeQuery(id+"F1.opExtrude","CAP_FACE",FACE,{"disambiguationData":[OSD([subQ1,sQuery(id+"F0.wireOp",EDGE,"E3"),sQuery(id+"F0.wireOp",EDGE,"E4.MirrorCS"),subQ0,sQuery(id+"F0.wireOp",EDGE,"QS45Ad1f-zS77-PmQo-UpQF-622HsvFARksc"),sQuery(id+"F0.wireOp",EDGE,"E7"),sQuery(id+"F0.wireOp",EDGE,"E8"),sQuery(id+"F0.wireOp",EDGE,"abd28260-5241-46c7-9a49-41b6c746b0a20.MirrorCS"),sQuery(id+"F0.wireOp",EDGE,"E10.MirrorCS"),sQuery(id+"F0.wireOp",EDGE,"273b9097-7943-4664-901e-a9dfdd62f2f80.MirrorCS"),sQuery(id+"F0.wireOp",EDGE,"E11")])],"isStart":true})]});}
            var Q16;
            {var subQ0=sQuery(id+"F0.wireOp",EDGE,"273b9097-7943-4664-901e-a9dfdd62f2f80.MirrorCS");Q16=makeQuery(id+"F2.opChamfer","BLEND_EDGE",EDGE,{"blendedFrom":[makeQuery(id+"F1.opExtrude","CAP_EDGE",EDGE,{"disambiguationData":[OSD([subQ0])],"isStart":true}),makeQuery(id+"F1.opExtrude","CAP_FACE",FACE,{"disambiguationData":[OSD([sQuery(id+"F0.wireOp",EDGE,"E2"),sQuery(id+"F0.wireOp",EDGE,"E3"),sQuery(id+"F0.wireOp",EDGE,"E4.MirrorCS"),sQuery(id+"F0.wireOp",EDGE,"E5.MirrorCS"),sQuery(id+"F0.wireOp",EDGE,"QS45Ad1f-zS77-PmQo-UpQF-622HsvFARksc"),sQuery(id+"F0.wireOp",EDGE,"E7"),sQuery(id+"F0.wireOp",EDGE,"E8"),sQuery(id+"F0.wireOp",EDGE,"abd28260-5241-46c7-9a49-41b6c746b0a20.MirrorCS"),sQuery(id+"F0.wireOp",EDGE,"E10.MirrorCS"),subQ0,sQuery(id+"F0.wireOp",EDGE,"E11")])],"isStart":true})],"blendedInto":[makeQuery(id+"F1.opExtrude","CAP_FACE",FACE,{"disambiguationData":[OSD([sQuery(id+"F0.wireOp",EDGE,"E2"),sQuery(id+"F0.wireOp",EDGE,"E3"),sQuery(id+"F0.wireOp",EDGE,"E4.MirrorCS"),sQuery(id+"F0.wireOp",EDGE,"E5.MirrorCS"),sQuery(id+"F0.wireOp",EDGE,"QS45Ad1f-zS77-PmQo-UpQF-622HsvFARksc"),sQuery(id+"F0.wireOp",EDGE,"E7"),sQuery(id+"F0.wireOp",EDGE,"E8"),sQuery(id+"F0.wireOp",EDGE,"abd28260-5241-46c7-9a49-41b6c746b0a20.MirrorCS"),sQuery(id+"F0.wireOp",EDGE,"E10.MirrorCS"),subQ0,sQuery(id+"F0.wireOp",EDGE,"E11")])],"isStart":true})]});}
            var Q17;
            {var subQ0=sQuery(id+"F0.wireOp",EDGE,"E13");Q17=makeQuery(id+"F2.opChamfer","BLEND_EDGE",EDGE,{"blendedFrom":[makeQuery(id+"F1.opExtrude","CAP_EDGE",EDGE,{"disambiguationData":[OSD([subQ0])],"isStart":true}),makeQuery(id+"F1.opExtrude","CAP_FACE",FACE,{"disambiguationData":[OSD([sQuery(id+"F0.wireOp",EDGE,"E2"),sQuery(id+"F0.wireOp",EDGE,"E3"),sQuery(id+"F0.wireOp",EDGE,"E4.MirrorCS"),sQuery(id+"F0.wireOp",EDGE,"E5.MirrorCS"),sQuery(id+"F0.wireOp",EDGE,"E7"),sQuery(id+"F0.wireOp",EDGE,"E8"),sQuery(id+"F0.wireOp",EDGE,"E10.MirrorCS"),sQuery(id+"F0.wireOp",EDGE,"E11"),sQuery(id+"F0.wireOp",EDGE,"E12"),subQ0,sQuery(id+"F0.wireOp",EDGE,"E14"),sQuery(id+"F0.wireOp",EDGE,"E15"),sQuery(id+"F0.wireOp",EDGE,"E16"),sQuery(id+"F0.wireOp",EDGE,"E17"),sQuery(id+"F0.wireOp",EDGE,"E18"),sQuery(id+"F0.wireOp",EDGE,"E19"),sQuery(id+"F0.wireOp",EDGE,"E20")])],"isStart":true})],"blendedInto":[makeQuery(id+"F1.opExtrude","CAP_FACE",FACE,{"disambiguationData":[OSD([sQuery(id+"F0.wireOp",EDGE,"E2"),sQuery(id+"F0.wireOp",EDGE,"E3"),sQuery(id+"F0.wireOp",EDGE,"E4.MirrorCS"),sQuery(id+"F0.wireOp",EDGE,"E5.MirrorCS"),sQuery(id+"F0.wireOp",EDGE,"E7"),sQuery(id+"F0.wireOp",EDGE,"E8"),sQuery(id+"F0.wireOp",EDGE,"E10.MirrorCS"),sQuery(id+"F0.wireOp",EDGE,"E11"),sQuery(id+"F0.wireOp",EDGE,"E12"),subQ0,sQuery(id+"F0.wireOp",EDGE,"E14"),sQuery(id+"F0.wireOp",EDGE,"E15"),sQuery(id+"F0.wireOp",EDGE,"E16"),sQuery(id+"F0.wireOp",EDGE,"E17"),sQuery(id+"F0.wireOp",EDGE,"E18"),sQuery(id+"F0.wireOp",EDGE,"E19"),sQuery(id+"F0.wireOp",EDGE,"E20")])],"isStart":true})]});}
            fillet(context, id + "F3", {"entities" : qUnion([Q0, Q1, Q2, Q3, Q4, Q5, Q6, Q7, Q8, Q9, Q10, Q11, Q12, Q13, Q14, Q15, Q16, Q17]), "radius" : 2.54 * mm, "tangentPropagation" : true, "allowEdgeOverflow" : false});
        }
        {
            var Q0;
            Q0=makeQuery(id+"F1.opExtrude","SWEPT_EDGE",EDGE,{"disambiguationData":[OSD([sQuery(id+"F0.wireOp",EDGE,"E3"),sQuery(id+"F0.wireOp",EDGE,"QS45Ad1f-zS77-PmQo-UpQF-622HsvFARksc")])]});
            var Q1;
            Q1=makeQuery(id+"F1.opExtrude","SWEPT_EDGE",EDGE,{"disambiguationData":[OSD([sQuery(id+"F0.wireOp",EDGE,"E3"),sQuery(id+"F0.wireOp",EDGE,"E8")])]});
            var Q2;
            Q2=makeQuery(id+"F1.opExtrude","SWEPT_EDGE",EDGE,{"disambiguationData":[OSD([sQuery(id+"F0.wireOp",EDGE,"E4.MirrorCS"),sQuery(id+"F0.wireOp",EDGE,"abd28260-5241-46c7-9a49-41b6c746b0a20.MirrorCS")])]});
            var Q3;
            Q3=makeQuery(id+"F1.opExtrude","SWEPT_EDGE",EDGE,{"disambiguationData":[OSD([sQuery(id+"F0.wireOp",EDGE,"E4.MirrorCS"),sQuery(id+"F0.wireOp",EDGE,"E10.MirrorCS")])]});
            var Q4;
            Q4=makeQuery(id+"F1.opExtrude","SWEPT_EDGE",EDGE,{"disambiguationData":[OSD([sQuery(id+"F0.wireOp",EDGE,"E5.MirrorCS"),sQuery(id+"F0.wireOp",EDGE,"273b9097-7943-4664-901e-a9dfdd62f2f80.MirrorCS")])]});
            var Q5;
            Q5=makeQuery(id+"F1.opExtrude","SWEPT_EDGE",EDGE,{"disambiguationData":[OSD([sQuery(id+"F0.wireOp",EDGE,"E2"),sQuery(id+"F0.wireOp",EDGE,"E7")])]});
            fillet(context, id + "F4", {"entities" : qUnion([Q0, Q1, Q2, Q3, Q4, Q5]), "radius" : 2.3 * mm, "tangentPropagation" : true, "allowEdgeOverflow" : false});
        }
        {
            var Q0;
            Q0=makeQuery(id+"F1.opExtrude","SWEPT_EDGE",EDGE,{"disambiguationData":[OSD([sQuery(id+"F0.wireOp",EDGE,"E12"),sQuery(id+"F0.wireOp",EDGE,"E13")])]});
            var Q1;
            Q1=makeQuery(id+"F1.opExtrude","SWEPT_EDGE",EDGE,{"disambiguationData":[OSD([sQuery(id+"F0.wireOp",EDGE,"E15"),sQuery(id+"F0.wireOp",EDGE,"E16")])]});
            var Q2;
            Q2=makeQuery(id+"F1.opExtrude","SWEPT_EDGE",EDGE,{"disambiguationData":[OSD([sQuery(id+"F0.wireOp",EDGE,"E18"),sQuery(id+"F0.wireOp",EDGE,"E19")])]});
            fillet(context, id + "F5", {"entities" : qUnion([Q0, Q1, Q2]), "radius" : 1.27 * mm, "tangentPropagation" : true, "allowEdgeOverflow" : false});
        }
    });
